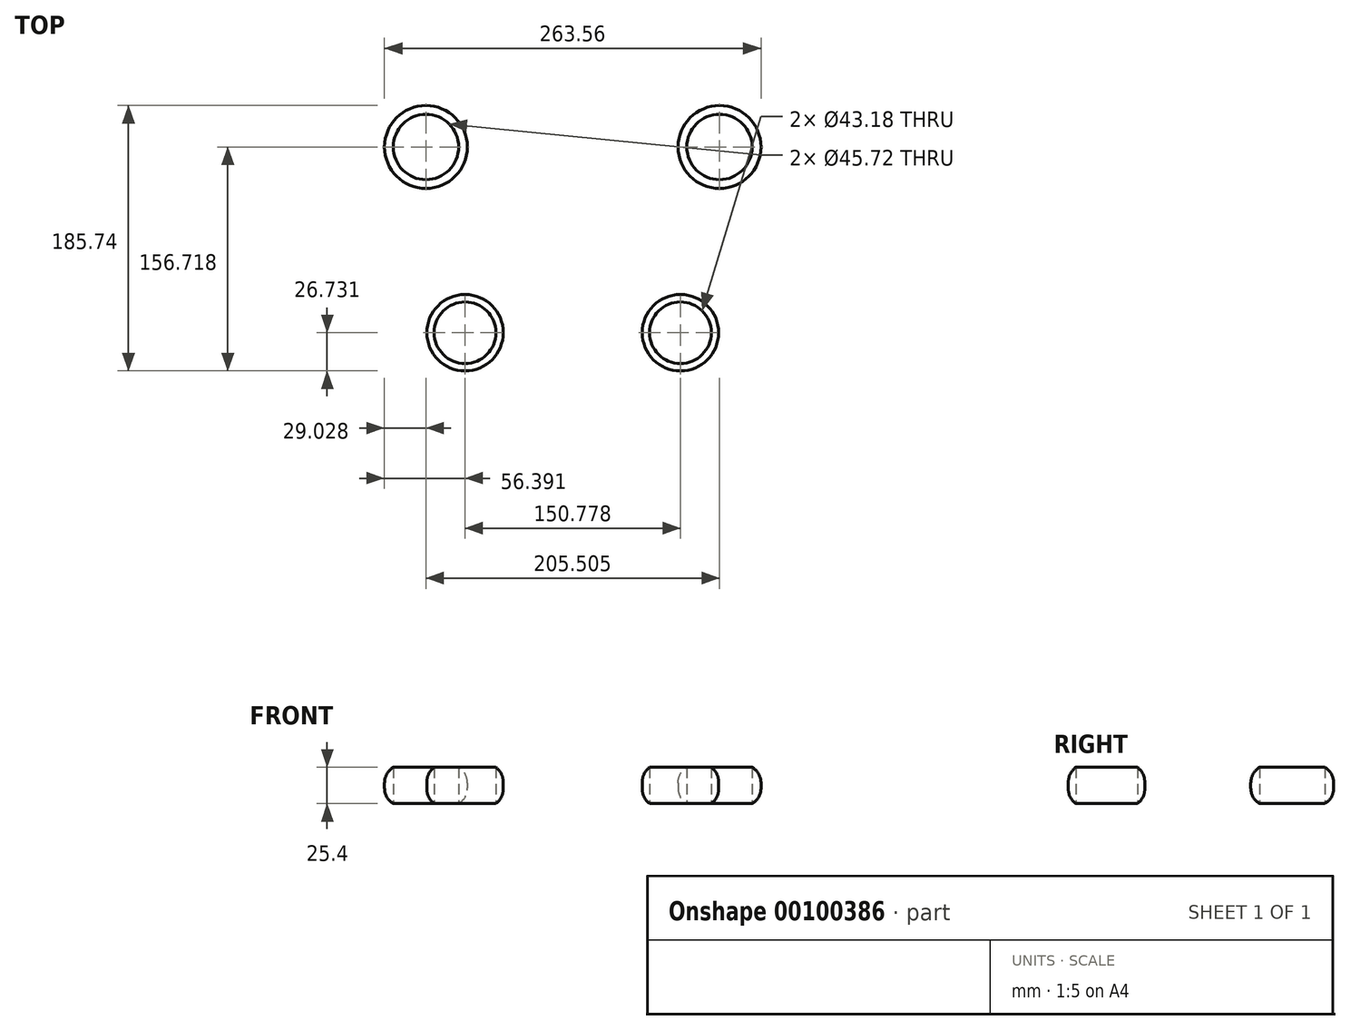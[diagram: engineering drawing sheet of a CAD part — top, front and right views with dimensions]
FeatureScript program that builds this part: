
annotation { "Feature Type Name" : "Feature", "Feature Type Description" : "" }
export const myFeature = defineFeature(function(context is Context, id is Id, definition is map)
    precondition{}
    {
        {
            var Q0;
            Q0=qCreatedBy(makeId("Top.planeOp"),FACE);
            var sketch = newSketch(context, id + "F0", { "sketchPlane" : qUnion([Q0])});
            skCircle(sketch, "E0", {"center": v(-102.75, 60.78) * mm, "radius": 29.03 * mm});
            skPoint(sketch, "E0.first.point", {"position": v(-73.93, 64.2) * mm});
            skPoint(sketch, "E0.second.point", {"position": v(-131.7, 58.54) * mm});
            skPoint(sketch, "E0.third.point", {"position": v(-110.55, 32.82) * mm});
            skCircle(sketch, "E1.MirrorC", {"center": v(102.75, 60.78) * mm, "radius": 29.03 * mm});
            skSolve(sketch);
        }
        {
            var Q0;
            Q0=qCreatedBy(makeId("Top.planeOp"),FACE);
            var sketch = newSketch(context, id + "F1", { "sketchPlane" : qUnion([Q0])});
            skCircle(sketch, "E2", {"center": v(-75.39, -69.2) * mm, "radius": 26.73 * mm});
            skPoint(sketch, "E2.first.point", {"position": v(-49.37, -63.07) * mm});
            skPoint(sketch, "E2.second.point", {"position": v(-101.16, -76.33) * mm});
            skPoint(sketch, "E2.third.point", {"position": v(-59.23, -90.5) * mm});
            skCircle(sketch, "E3.MirrorC", {"center": v(75.39, -69.2) * mm, "radius": 26.73 * mm});
            skSolve(sketch);
        }
        {
            var Q0;
            Q0 = qSketchRegion(id + "F0", true);
            var Q1;
            Q1 = qSketchRegion(id + "F1", true);
            extrude(context, id + "F2", {"entities" : qUnion([Q0, Q1]), "depth" : 25.4 * mm});
        }
        {
            var Q0;
            Q0=sQuery(id+"F0.wireOp",VERTEX,"E1.MirrorC.center");
            var Q1;
            Q1=sQuery(id+"F0.wireOp",VERTEX,"E0.center");
            var Q2;
            Q2=makeQuery(id+"F2.opExtrude","SWEPT_BODY",BODY,{"disambiguationData":[OSD([sQuery(id+"F0.wireOp",EDGE,"E1.MirrorC")])]});
            var Q3;
            Q3=makeQuery(id+"F2.opExtrude","SWEPT_BODY",BODY,{"disambiguationData":[OSD([sQuery(id+"F0.wireOp",EDGE,"E0")])]});
            hole(context, id + "F3", {"style" : HoleStyle.SIMPLE, "endStyle" : HoleEndStyle.THROUGH, "oppositeDirection" : true, "holeDiameter" : 45.72 * mm, "locations" : qUnion([Q0, Q1]), "scope" : qUnion([Q2, Q3]), "isTappedThrough" : true});
        }
        {
            var Q0;
            Q0=sQuery(id+"F1.wireOp",VERTEX,"E3.MirrorC.center");
            var Q1;
            Q1=sQuery(id+"F1.wireOp",VERTEX,"E2.center");
            var Q2;
            Q2=makeQuery(id+"F2.opExtrude","SWEPT_BODY",BODY,{"disambiguationData":[OSD([sQuery(id+"F1.wireOp",EDGE,"E3.MirrorC")])]});
            var Q3;
            Q3=makeQuery(id+"F2.opExtrude","SWEPT_BODY",BODY,{"disambiguationData":[OSD([sQuery(id+"F1.wireOp",EDGE,"E2")])]});
            hole(context, id + "F4", {"style" : HoleStyle.SIMPLE, "endStyle" : HoleEndStyle.THROUGH, "oppositeDirection" : true, "holeDiameter" : 43.18 * mm, "locations" : qUnion([Q0, Q1]), "scope" : qUnion([Q2, Q3]), "isTappedThrough" : true});
        }
        {
            var Q0;
            Q0=makeQuery(id+"F2.opExtrude","CAP_EDGE",EDGE,{"disambiguationData":[OSD([sQuery(id+"F0.wireOp",EDGE,"E1.MirrorC")])],"isStart":false});
            var Q1;
            Q1=makeQuery(id+"F2.opExtrude","CAP_EDGE",EDGE,{"disambiguationData":[OSD([sQuery(id+"F0.wireOp",EDGE,"E1.MirrorC")])],"isStart":true});
            var Q2;
            Q2=makeQuery(id+"F2.opExtrude","CAP_EDGE",EDGE,{"disambiguationData":[OSD([sQuery(id+"F0.wireOp",EDGE,"E0")])],"isStart":false});
            var Q3;
            Q3=makeQuery(id+"F2.opExtrude","CAP_EDGE",EDGE,{"disambiguationData":[OSD([sQuery(id+"F0.wireOp",EDGE,"E0")])],"isStart":true});
            var Q4;
            Q4=makeQuery(id+"F2.opExtrude","CAP_EDGE",EDGE,{"disambiguationData":[OSD([sQuery(id+"F1.wireOp",EDGE,"E2")])],"isStart":false});
            var Q5;
            Q5=makeQuery(id+"F2.opExtrude","CAP_EDGE",EDGE,{"disambiguationData":[OSD([sQuery(id+"F1.wireOp",EDGE,"E2")])],"isStart":true});
            var Q6;
            Q6=makeQuery(id+"F2.opExtrude","CAP_EDGE",EDGE,{"disambiguationData":[OSD([sQuery(id+"F1.wireOp",EDGE,"E3.MirrorC")])],"isStart":false});
            var Q7;
            Q7=makeQuery(id+"F2.opExtrude","CAP_EDGE",EDGE,{"disambiguationData":[OSD([sQuery(id+"F1.wireOp",EDGE,"E3.MirrorC")])],"isStart":true});
            fillet(context, id + "F5", {"entities" : qUnion([Q0, Q1, Q2, Q3, Q4, Q5, Q6, Q7]), "radius" : 12.7 * mm, "tangentPropagation" : true, "allowEdgeOverflow" : false});
        }
    });
